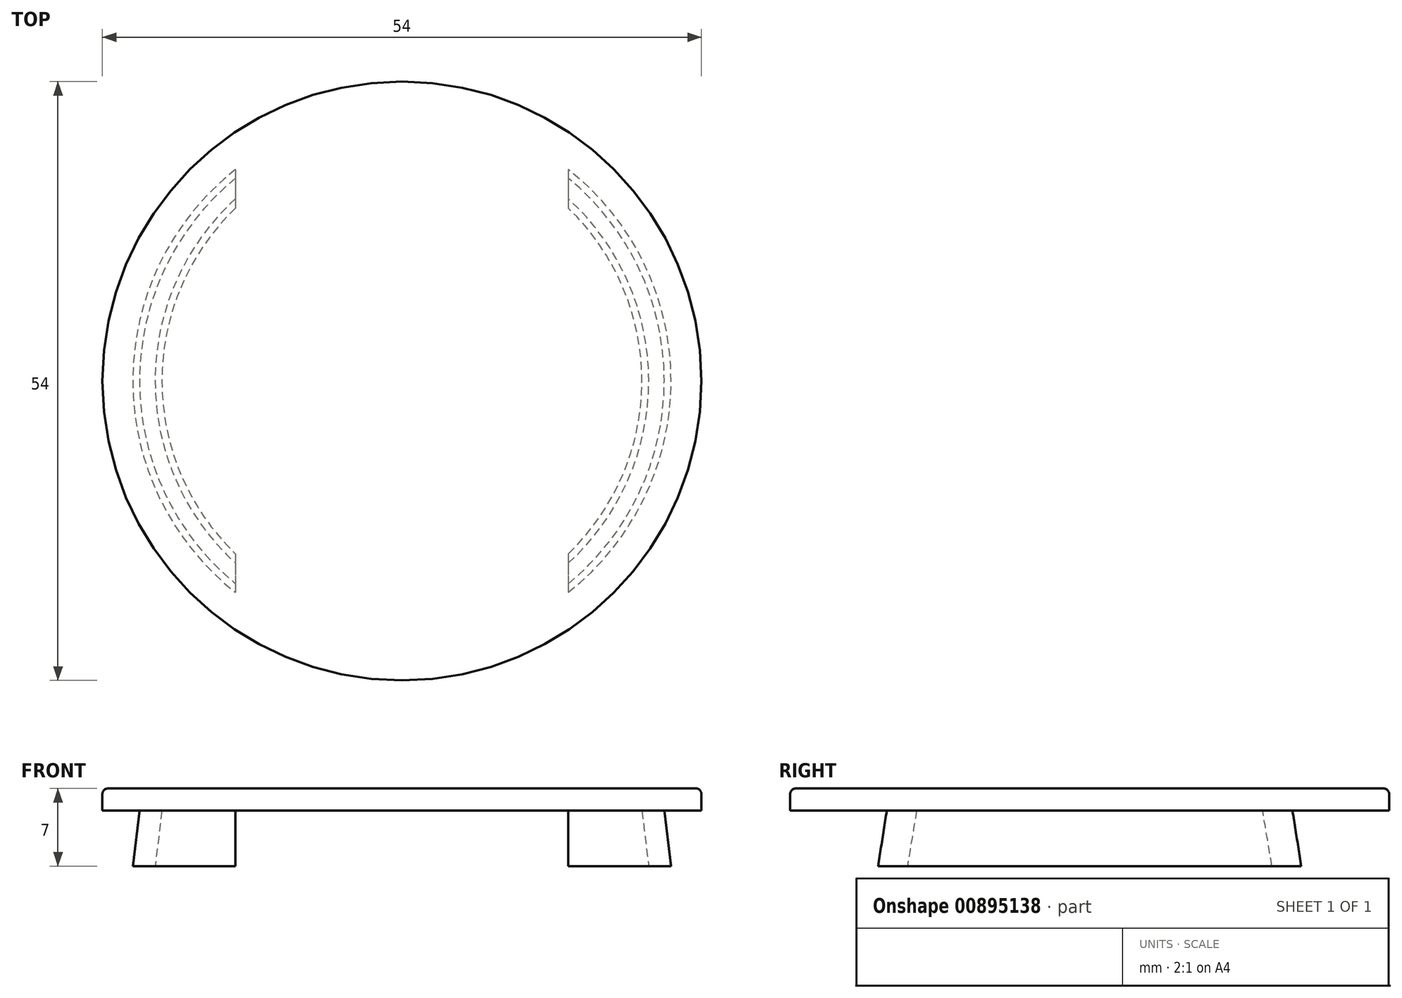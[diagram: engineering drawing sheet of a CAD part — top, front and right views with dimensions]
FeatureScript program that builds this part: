
annotation { "Feature Type Name" : "Feature", "Feature Type Description" : "" }
export const myFeature = defineFeature(function(context is Context, id is Id, definition is map)
    precondition{}
    {
        {
            var Q0;
            Q0=qCreatedBy(makeId("Top.planeOp"),FACE);
            var sketch = newSketch(context, id + "F0", { "sketchPlane" : qUnion([Q0])});
            skCircle(sketch, "E0", {"center": v(0, 0) * mm, "radius": 27 * mm});
            skCircle(sketch, "E1", {"center": v(0, 0) * mm, "radius": 23.65 * mm});
            skSolve(sketch);
        }
        {
            var Q0;
            Q0=makeQuery(id+"F0.imprint","IMPRINT",FACE,{"disambiguationData":[TD([[makeQuery(id+"F0.imprint","IMPRINT",EDGE,{"derivedFrom":sQuery(id+"F0.wireOp",EDGE,"E0")}),1.0]])]});
            var Q1;
            Q1=makeQuery(id+"F0.imprint","IMPRINT",FACE,{"disambiguationData":[TD([[makeQuery(id+"F0.imprint","IMPRINT",EDGE,{"derivedFrom":sQuery(id+"F0.wireOp",EDGE,"E1")}),1.0]])]});
            extrude(context, id + "F1", {"entities" : qUnion([Q0, Q1]), "depth" : 2 * mm, "offsetDistance" : 25 * mm});
        }
        {
            var Q0;
            Q0=makeQuery(id+"F0.imprint","IMPRINT",FACE,{"disambiguationData":[TD([[makeQuery(id+"F0.imprint","IMPRINT",EDGE,{"derivedFrom":sQuery(id+"F0.wireOp",EDGE,"E1")}),1.0]])]});
            extrude(context, id + "F2", {"entities" : qUnion([Q0]), "operationType" : NewBodyOperationType.ADD, "oppositeDirection" : true, "depth" : 5 * mm, "offsetDistance" : 25 * mm, "hasDraft" : true, "draftAngle" : 7 * degree});
        }
        {
            var Q0;
            Q0=makeQuery(id+"F2.opExtrude","CAP_FACE",FACE,{"disambiguationData":[OSD([sQuery(id+"F0.wireOp",EDGE,"E1")])],"isStart":false});
            shell(context, id + "F3", {"entities" : qUnion([Q0]), "thickness" : 2 * mm});
        }
        {
            var Q0;
            Q0=qCreatedBy(makeId("Front.planeOp"),FACE);
            var sketch = newSketch(context, id + "F4", { "sketchPlane" : qUnion([Q0])});
            skLineSegment(sketch, "E2.bottom", {"start": v(0, 0) * mm, "end": v(15, 0) * mm});
            skLineSegment(sketch, "E2.top", {"start": v(0, -7.3) * mm, "end": v(15, -7.3) * mm});
            skLineSegment(sketch, "E2.left", {"start": v(0, 0) * mm, "end": v(0, -7.3) * mm});
            skLineSegment(sketch, "E2.right", {"start": v(15, 0) * mm, "end": v(15, -7.3) * mm});
            skLineSegment(sketch, "E3.MirrorCS", {"start": v(-15, 0) * mm, "end": v(-15, -7.3) * mm});
            skLineSegment(sketch, "E4.MirrorCS", {"start": v(0, -7.3) * mm, "end": v(-15, -7.3) * mm});
            skLineSegment(sketch, "E5.MirrorCS", {"start": v(0, 0) * mm, "end": v(-15, 0) * mm});
            skSolve(sketch);
        }
        {
            var Q0;
            Q0 = qSketchRegion(id + "F4", true);
            extrude(context, id + "F5", {"entities" : qUnion([Q0]), "operationType" : NewBodyOperationType.REMOVE, "oppositeDirection" : true, "depth" : 25 * mm, "offsetDistance" : 25 * mm, "hasSecondDirection" : true, "secondDirectionOppositeDirection" : false, "secondDirectionDepth" : 25 * mm});
        }
        {
            var Q0;
            Q0=makeQuery(id+"F1.opExtrude","CAP_EDGE",EDGE,{"disambiguationData":[OSD([sQuery(id+"F0.wireOp",EDGE,"E0")])],"isStart":false});
            fillet(context, id + "F6", {"entities" : qUnion([Q0]), "radius" : 0.5 * mm, "tangentPropagation" : true, "allowEdgeOverflow" : false});
        }
    });
